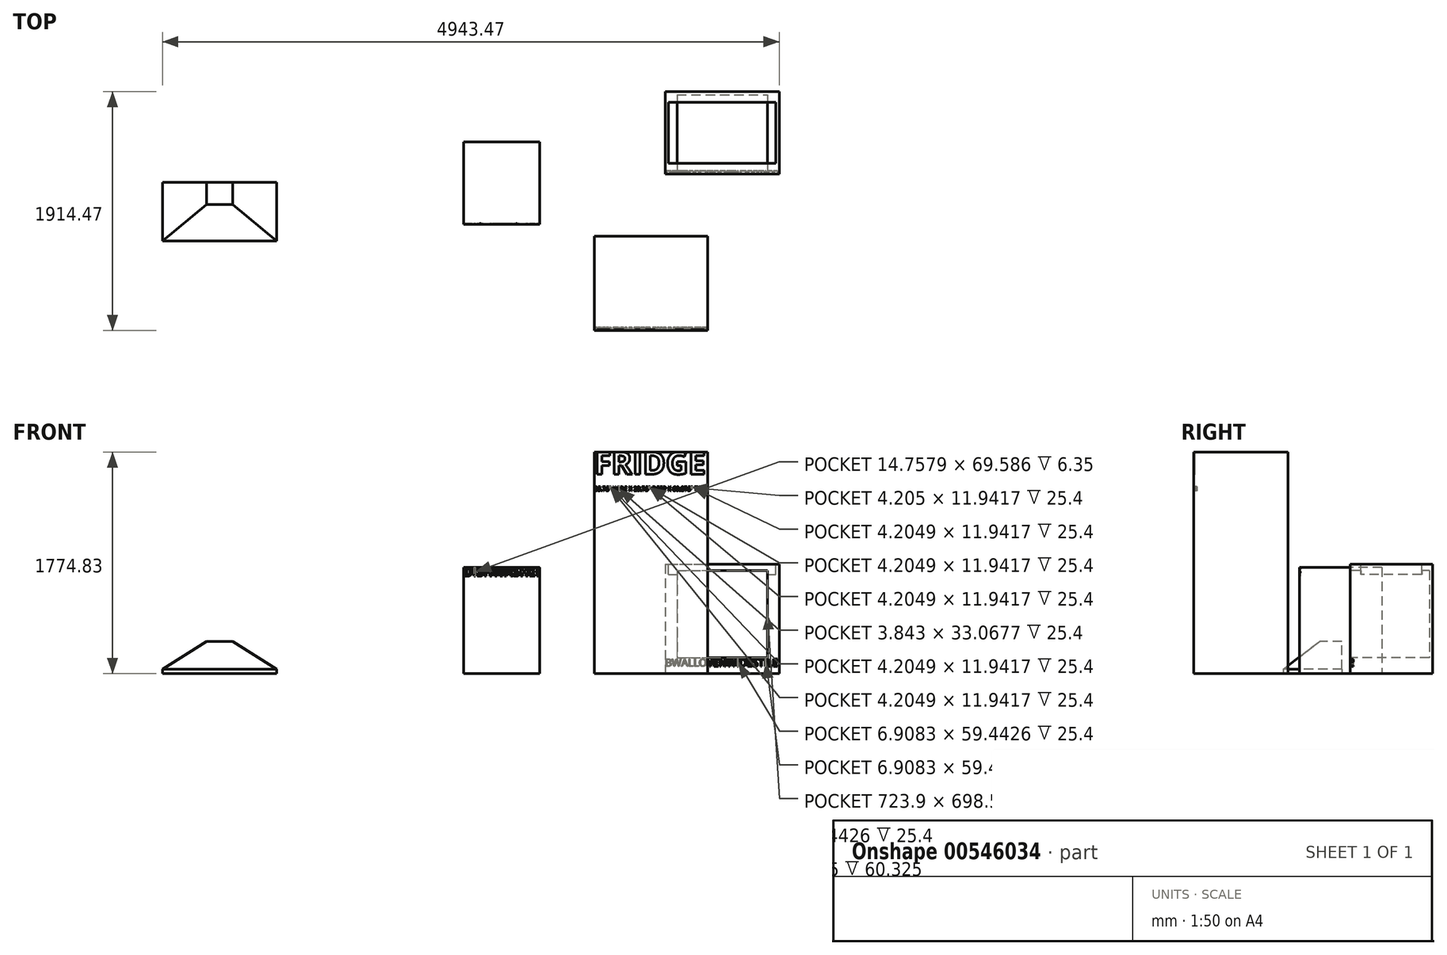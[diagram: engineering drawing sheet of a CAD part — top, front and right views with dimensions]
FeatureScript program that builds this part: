
annotation { "Feature Type Name" : "Feature", "Feature Type Description" : "" }
export const myFeature = defineFeature(function(context is Context, id is Id, definition is map)
    precondition{}
    {
        {
            var Q0;
            Q0=qCreatedBy(makeId("Top.planeOp"),FACE);
            var sketch = newSketch(context, id + "F0", { "sketchPlane" : qUnion([Q0])});
            skLineSegment(sketch, "E0.bottom", {"start": v(0, 0) * mm, "end": v(908.05, 0) * mm});
            skLineSegment(sketch, "E0.top", {"start": v(0, -755.65) * mm, "end": v(908.05, -755.65) * mm});
            skLineSegment(sketch, "E0.left", {"start": v(0, 0) * mm, "end": v(0, -755.65) * mm});
            skLineSegment(sketch, "E0.right", {"start": v(908.05, 0) * mm, "end": v(908.05, -755.65) * mm});
            skSolve(sketch);
        }
        {
            var Q0;
            Q0 = qSketchRegion(id + "F0", true);
            extrude(context, id + "F1", {"entities" : qUnion([Q0]), "depth" : 1774.82 * mm, "offsetDistance" : 25.4 * mm});
        }
        {
            var Q0;
            Q0=makeQuery(id+"F1.opExtrude","SWEPT_FACE",FACE,{"disambiguationData":[OSD([sQuery(id+"F0.wireOp",EDGE,"E0.top")])]});
            var sketch = newSketch(context, id + "F2", { "sketchPlane" : qUnion([Q0])});
            skText(sketch, "E1", { "text": "FRIDGE", "fontName": "OpenSans-Bold.ttf"});
            const initialGuessF2  = {"E1": [0, 1.59744, 1, 0, 0.18056]};
            skSetInitialGuess(sketch, initialGuessF2);
            skSolve(sketch);
        }
        {
            var Q0;
            Q0 = qSketchRegion(id + "F2", true);
            extrude(context, id + "F3", {"entities" : qUnion([Q0]), "operationType" : NewBodyOperationType.REMOVE, "oppositeDirection" : true, "depth" : 6.35 * mm, "offsetDistance" : 25.4 * mm});
        }
        {
            var Q0;
            Q0=qCreatedBy(makeId("Top.planeOp"),FACE);
            var sketch = newSketch(context, id + "F4", { "sketchPlane" : qUnion([Q0])});
            skLineSegment(sketch, "E2.bottom", {"start": v(-1047.42, 754.26) * mm, "end": v(-437.82, 754.26) * mm});
            skLineSegment(sketch, "E2.top", {"start": v(-1047.42, 93.86) * mm, "end": v(-437.82, 93.86) * mm});
            skLineSegment(sketch, "E2.left", {"start": v(-1047.42, 754.26) * mm, "end": v(-1047.42, 93.86) * mm});
            skLineSegment(sketch, "E2.right", {"start": v(-437.82, 754.26) * mm, "end": v(-437.82, 93.86) * mm});
            skSolve(sketch);
        }
        {
            var Q0;
            Q0 = qSketchRegion(id + "F4", true);
            extrude(context, id + "F5", {"entities" : qUnion([Q0]), "operationType" : NewBodyOperationType.ADD, "depth" : 850.9 * mm, "offsetDistance" : 25.4 * mm});
        }
        {
            var Q0;
            Q0=makeQuery(id+"F5.opExtrude","SWEPT_FACE",FACE,{"disambiguationData":[OSD([sQuery(id+"F4.wireOp",EDGE,"E2.top")])]});
            var sketch = newSketch(context, id + "F6", { "sketchPlane" : qUnion([Q0])});
            skText(sketch, "E3", { "text": "DISHWASHER", "fontName": "OpenSans-Bold.ttf"});
            const initialGuessF6  = {"E3": [-1.04742, 0.78072, 1, 0, 0.07018]};
            skSetInitialGuess(sketch, initialGuessF6);
            skSolve(sketch);
        }
        {
            var Q0;
            Q0 = qSketchRegion(id + "F6", true);
            extrude(context, id + "F7", {"entities" : qUnion([Q0]), "operationType" : NewBodyOperationType.REMOVE, "oppositeDirection" : true, "depth" : 6.35 * mm, "offsetDistance" : 25.4 * mm});
        }
        {
            var Q0;
            Q0=qCreatedBy(makeId("Top.planeOp"),FACE);
            var sketch = newSketch(context, id + "F8", { "sketchPlane" : qUnion([Q0])});
            skLineSegment(sketch, "E4.bottom", {"start": v(566.89, 1158.82) * mm, "end": v(1481.29, 1158.82) * mm});
            skLineSegment(sketch, "E4.top", {"start": v(566.89, 498.42) * mm, "end": v(1481.29, 498.42) * mm});
            skLineSegment(sketch, "E4.left", {"start": v(566.89, 1158.82) * mm, "end": v(566.89, 498.42) * mm});
            skLineSegment(sketch, "E4.right", {"start": v(1481.29, 1158.82) * mm, "end": v(1481.29, 498.42) * mm});
            skSolve(sketch);
        }
        {
            var Q0;
            Q0 = qSketchRegion(id + "F8", true);
            extrude(context, id + "F9", {"entities" : qUnion([Q0]), "depth" : 876.3 * mm, "offsetDistance" : 25.4 * mm});
        }
        {
            var Q0;
            Q0=qCreatedBy(makeId("Top.planeOp"),FACE);
            var sketch = newSketch(context, id + "F10", { "sketchPlane" : qUnion([Q0])});
            skLineSegment(sketch, "E5.bottom", {"start": v(-3462.18, 432.77) * mm, "end": v(-2547.78, 432.77) * mm});
            skLineSegment(sketch, "E5.top", {"start": v(-3462.18, -37.13) * mm, "end": v(-2547.78, -37.13) * mm});
            skLineSegment(sketch, "E5.left", {"start": v(-3462.18, 432.77) * mm, "end": v(-3462.18, -37.13) * mm});
            skLineSegment(sketch, "E5.right", {"start": v(-2547.78, 432.77) * mm, "end": v(-2547.78, -37.13) * mm});
            skSolve(sketch);
        }
        {
            var Q0;
            Q0 = qSketchRegion(id + "F10", true);
            extrude(context, id + "F11", {"entities" : qUnion([Q0]), "depth" : 34.92 * mm, "offsetDistance" : 25.4 * mm});
        }
        {
            var Q0;
            Q0=makeQuery(id+"F11.opExtrude","CAP_FACE",FACE,{"disambiguationData":[OSD([sQuery(id+"F10.wireOp",EDGE,"E5.bottom"),sQuery(id+"F10.wireOp",EDGE,"E5.top"),sQuery(id+"F10.wireOp",EDGE,"E5.left"),sQuery(id+"F10.wireOp",EDGE,"E5.right")])],"isStart":false});
            var sketch = newSketch(context, id + "F12", { "sketchPlane" : qUnion([Q0])});
            skLineSegment(sketch, "E6.bottom", {"start": v(-3462.18, 432.77) * mm, "end": v(-2547.78, 432.77) * mm});
            skLineSegment(sketch, "E6.top", {"start": v(-3462.18, -37.13) * mm, "end": v(-2547.78, -37.13) * mm});
            skLineSegment(sketch, "E6.left", {"start": v(-3462.18, 432.77) * mm, "end": v(-3462.18, -37.13) * mm});
            skLineSegment(sketch, "E6.right", {"start": v(-2547.78, 432.77) * mm, "end": v(-2547.78, -37.13) * mm});
            skSolve(sketch);
        }
        {
            var Q0;
            Q0=makeQuery(id+"F12.imprint","IMPRINT",FACE,{"disambiguationData":[TD([[makeQuery(id+"F12.imprint","IMPRINT",EDGE,{"derivedFrom":sQuery(id+"F12.wireOp",EDGE,"E6.bottom")}),-1.0]])]});
            cPlane(context, id + "F13", {"entities" : qUnion([Q0]), "cplaneType" : CPlaneType.OFFSET, "offset" : 222.25 * mm, "width" : 152.4 * mm, "height" : 152.4 * mm});
        }
        {
            var Q0;
            Q0=qCreatedBy(id+"F13.planeOp",FACE);
            var sketch = newSketch(context, id + "F14", { "sketchPlane" : qUnion([Q0])});
            skLineSegment(sketch, "E7.bottom", {"start": v(-3109.76, 432.77) * mm, "end": v(-2900.2, 432.77) * mm});
            skLineSegment(sketch, "E7.top", {"start": v(-3109.76, 253.38) * mm, "end": v(-2900.2, 253.38) * mm});
            skLineSegment(sketch, "E7.left", {"start": v(-3109.76, 432.77) * mm, "end": v(-3109.76, 253.38) * mm});
            skLineSegment(sketch, "E7.right", {"start": v(-2900.2, 432.77) * mm, "end": v(-2900.2, 253.38) * mm});
            skLineSegment(sketch, "E8", {"start": v(-3004.98, 253.38) * mm, "end": v(-3004.98, -37.13) * mm, "construction": true});
            skSolve(sketch);
        }
        {
            var Q1;
            Q1=makeQuery(id+"F12.imprint","IMPRINT",FACE,{"disambiguationData":[TD([[makeQuery(id+"F12.imprint","IMPRINT",EDGE,{"derivedFrom":sQuery(id+"F12.wireOp",EDGE,"E6.bottom")}),-1.0]])]});
            var Q2;
            Q2=makeQuery(id+"F14.imprint","IMPRINT",FACE,{"disambiguationData":[TD([[makeQuery(id+"F14.imprint","IMPRINT",EDGE,{"derivedFrom":sQuery(id+"F14.wireOp",EDGE,"E7.bottom")}),-1.0]])]});
            loft(context, id + "F15", {"operationType" : NewBodyOperationType.ADD, "sheetProfilesArray" : [{ "sheetProfileEntities" : qUnion([Q1]) }, { "sheetProfileEntities" : qUnion([Q2]) }]});
        }
        {
            var Q0;
            {var subQ0=sQuery(id+"F0.wireOp",EDGE,"E0.left");var subQ2=sQuery(id+"F0.wireOp",EDGE,"E0.top");Q0=makeQuery(id+"F3.boolean.opBoolean","SPLIT",FACE,{"disambiguationData":[TD([makeQuery(id+"F1.opExtrude","SWEPT_FACE",FACE,{"disambiguationData":[OSD([subQ0])]})])],"derivedFrom":makeQuery(id+"F1.opExtrude","SWEPT_FACE",FACE,{"disambiguationData":[OSD([subQ2])]})});}
            var sketch = newSketch(context, id + "F16", { "sketchPlane" : qUnion([Q0])});
            skText(sketch, "E9", { "text": "35.75\" WIDE X 29.75\" DEEP X 69.875\" TALL", "fontName": "OpenSans-Regular.ttf"});
            const initialGuessF16  = {"E9": [0, 1.46433, 1, 0, 0.03335]};
            skSetInitialGuess(sketch, initialGuessF16);
            skSolve(sketch);
        }
        {
            var Q0;
            Q0 = qSketchRegion(id + "F16", true);
            extrude(context, id + "F17", {"entities" : qUnion([Q0]), "operationType" : NewBodyOperationType.REMOVE, "oppositeDirection" : true, "depth" : 25.4 * mm, "offsetDistance" : 25.4 * mm});
        }
        {
            var Q0;
            {var subQ1=sQuery(id+"F8.wireOp",EDGE,"E4.left");var subQ2=sQuery(id+"F8.wireOp",EDGE,"E4.top");Q0=makeQuery(id+"FCEN8T9ya4fGfJc_3.boolean.opBoolean","SPLIT",FACE,{"disambiguationData":[TD([makeQuery(id+"F9.opExtrude","SWEPT_FACE",FACE,{"disambiguationData":[OSD([subQ1])]})])],"derivedFrom":makeQuery(id+"F9.opExtrude","SWEPT_FACE",FACE,{"disambiguationData":[OSD([subQ2])]})});}
            var sketch = newSketch(context, id + "F18", { "sketchPlane" : qUnion([Q0])});
            skText(sketch, "E10", { "text": "BWALLOVENWIDESTILES", "fontName": "OpenSans-Regular.ttf"});
            const initialGuessF18  = {"E10": [0.56689, 0.05795, 1, 0, 0.05995]};
            skSetInitialGuess(sketch, initialGuessF18);
            skSolve(sketch);
        }
        {
            var Q0;
            Q0 = qSketchRegion(id + "F18", true);
            extrude(context, id + "F19", {"entities" : qUnion([Q0]), "operationType" : NewBodyOperationType.REMOVE, "oppositeDirection" : true, "depth" : 25.4 * mm, "offsetDistance" : 25.4 * mm});
        }
        {
            var Q0;
            Q0=makeQuery(id+"F9.opExtrude","CAP_FACE",FACE,{"disambiguationData":[OSD([sQuery(id+"F8.wireOp",EDGE,"E4.bottom"),sQuery(id+"F8.wireOp",EDGE,"E4.top"),sQuery(id+"F8.wireOp",EDGE,"E4.left"),sQuery(id+"F8.wireOp",EDGE,"E4.right")])],"isStart":false});
            var sketch = newSketch(context, id + "F20", { "sketchPlane" : qUnion([Q0])});
            skLineSegment(sketch, "E11.bottom", {"start": v(593.88, 1073.1) * mm, "end": v(1454.3, 1073.1) * mm});
            skLineSegment(sketch, "E11.top", {"start": v(593.88, 584.14) * mm, "end": v(1454.3, 584.14) * mm});
            skLineSegment(sketch, "E11.left", {"start": v(593.88, 1073.1) * mm, "end": v(593.88, 584.14) * mm});
            skLineSegment(sketch, "E11.right", {"start": v(1454.3, 1073.1) * mm, "end": v(1454.3, 584.14) * mm});
            skLineSegment(sketch, "E12", {"start": v(1024.09, 1073.1) * mm, "end": v(1024.09, 1158.82) * mm, "construction": true});
            skLineSegment(sketch, "E13", {"start": v(593.88, 828.62) * mm, "end": v(566.89, 828.62) * mm, "construction": true});
            skSolve(sketch);
        }
        {
            var Q0;
            Q0 = qSketchRegion(id + "F20", true);
            extrude(context, id + "F21", {"entities" : qUnion([Q0]), "operationType" : NewBodyOperationType.REMOVE, "oppositeDirection" : true, "depth" : 82.55 * mm, "offsetDistance" : 25.4 * mm});
        }
        {
            var Q0;
            {var subQ1=sQuery(id+"F8.wireOp",EDGE,"E4.left");var subQ2=sQuery(id+"F8.wireOp",EDGE,"E4.top");Q0=makeQuery(id+"F19.boolean.opBoolean","SPLIT",FACE,{"disambiguationData":[TD([makeQuery(id+"F9.opExtrude","SWEPT_FACE",FACE,{"disambiguationData":[OSD([subQ1])]})])],"derivedFrom":makeQuery(id+"F9.opExtrude","SWEPT_FACE",FACE,{"disambiguationData":[OSD([subQ2])]})});}
            var sketch = newSketch(context, id + "F22", { "sketchPlane" : qUnion([Q0])});
            skLineSegment(sketch, "E14.bottom", {"start": v(662.14, 825.5) * mm, "end": v(1386.04, 825.5) * mm});
            skLineSegment(sketch, "E14.top", {"start": v(662.14, 127) * mm, "end": v(1386.04, 127) * mm});
            skLineSegment(sketch, "E14.left", {"start": v(662.14, 825.5) * mm, "end": v(662.14, 127) * mm});
            skLineSegment(sketch, "E14.right", {"start": v(1386.04, 825.5) * mm, "end": v(1386.04, 127) * mm});
            skLineSegment(sketch, "E15", {"start": v(1024.09, 876.3) * mm, "end": v(1024.09, 825.5) * mm, "construction": true});
            skSolve(sketch);
        }
        {
            var Q0;
            Q0 = qSketchRegion(id + "F22", true);
            extrude(context, id + "F23", {"entities" : qUnion([Q0]), "operationType" : NewBodyOperationType.REMOVE, "oppositeDirection" : true, "depth" : 635 * mm, "offsetDistance" : 25.4 * mm});
        }
    });
